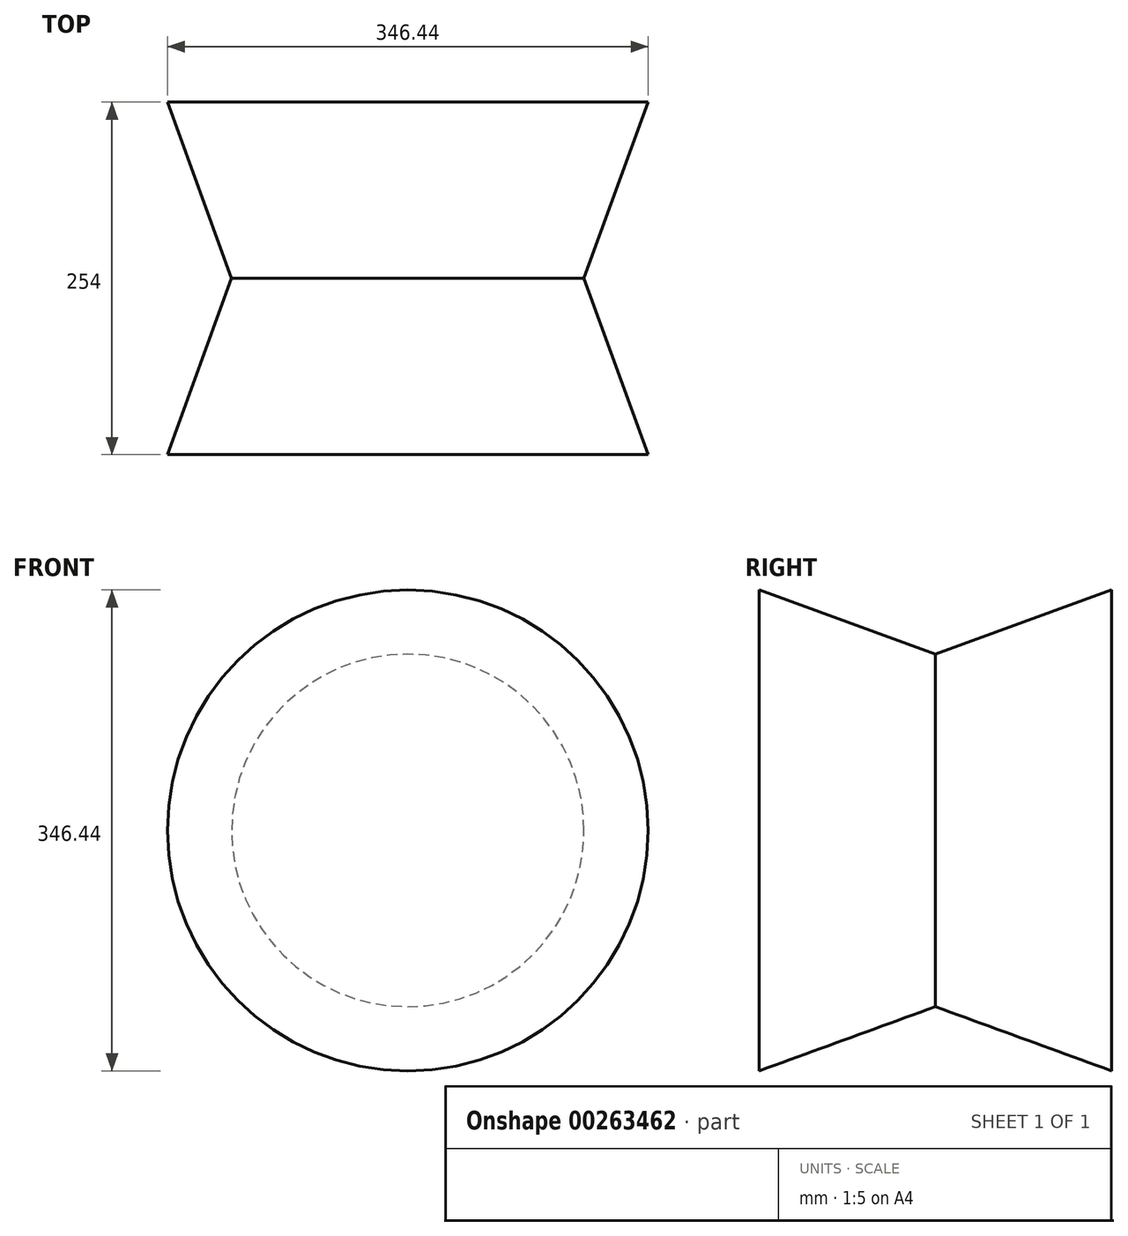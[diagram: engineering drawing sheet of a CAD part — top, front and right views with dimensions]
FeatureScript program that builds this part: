
annotation { "Feature Type Name" : "Feature", "Feature Type Description" : "" }
export const myFeature = defineFeature(function(context is Context, id is Id, definition is map)
    precondition{}
    {
        {
            var Q0;
            Q0=qCreatedBy(makeId("Front.planeOp"),FACE);
            var sketch = newSketch(context, id + "F0", { "sketchPlane" : qUnion([Q0])});
            skCircle(sketch, "E0", {"center": v(0, 0) * mm, "radius": 127 * mm});
            skSolve(sketch);
        }
        {
            var Q0;
            Q0=makeQuery(id+"F0.imprint","IMPRINT",FACE,{"disambiguationData":[TD([[makeQuery(id+"F0.imprint","IMPRINT",EDGE,{"derivedFrom":sQuery(id+"F0.wireOp",EDGE,"E0")}),1.0]])]});
            extrude(context, id + "F1", {"entities" : qUnion([Q0]), "endBound" : BoundingType.SYMMETRIC, "depth" : 254 * mm, "hasDraft" : true, "draftAngle" : 20 * degree});
        }
    });
